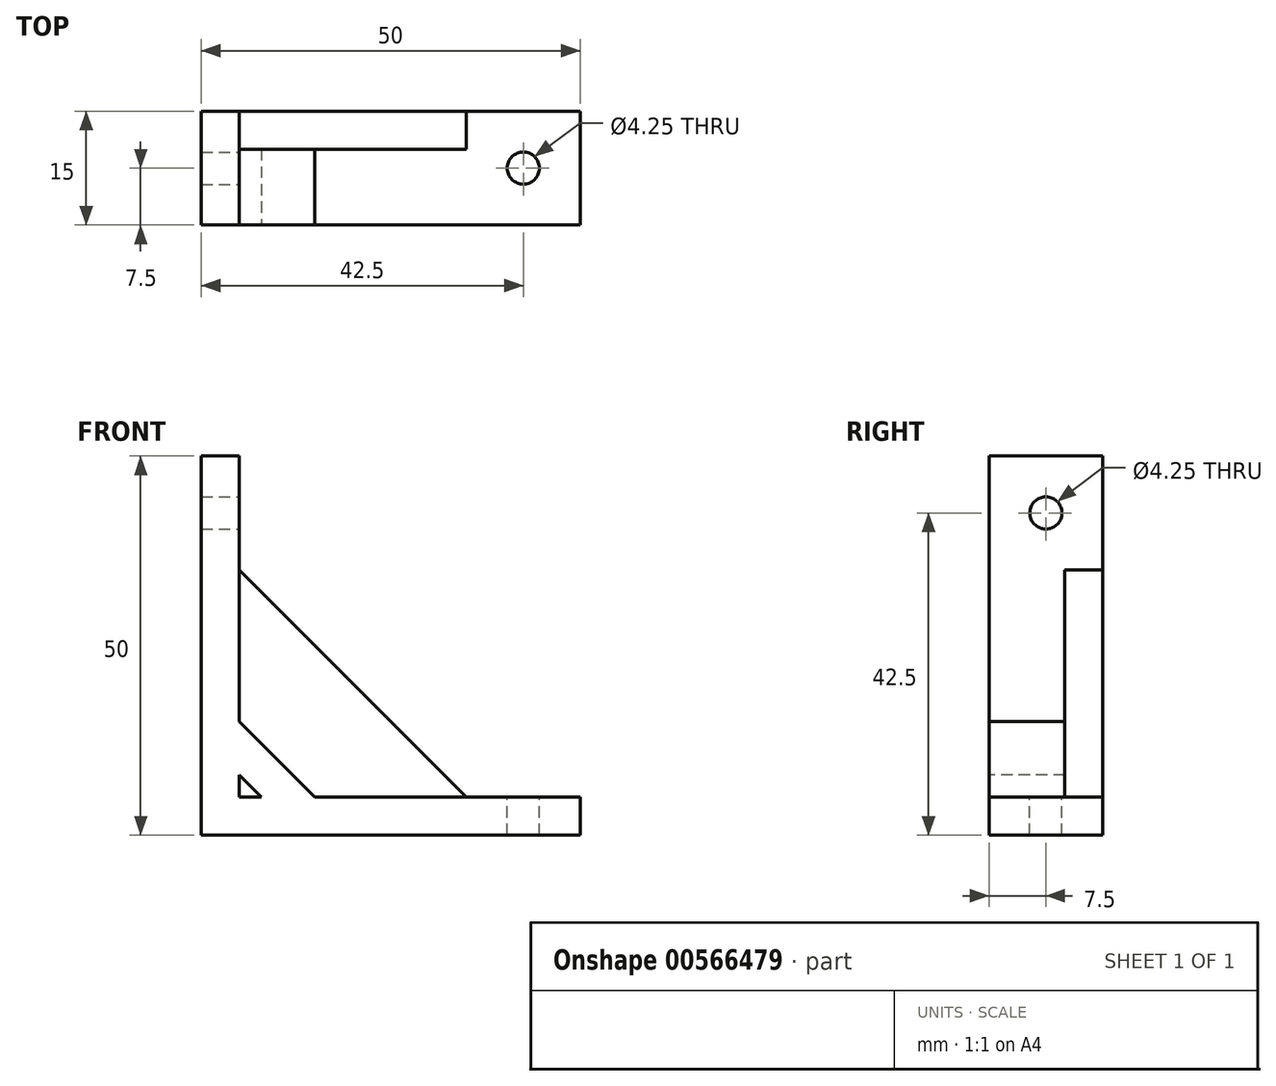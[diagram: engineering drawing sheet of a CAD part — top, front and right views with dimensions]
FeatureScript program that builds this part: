
annotation { "Feature Type Name" : "Feature", "Feature Type Description" : "" }
export const myFeature = defineFeature(function(context is Context, id is Id, definition is map)
    precondition{}
    {
        {
            var Q0;
            Q0=qCreatedBy(makeId("Front.planeOp"),FACE);
            var sketch = newSketch(context, id + "F0", { "sketchPlane" : qUnion([Q0])});
            skLineSegment(sketch, "E0", {"start": v(0, 50) * mm, "end": v(0, 0) * mm});
            skLineSegment(sketch, "E1", {"start": v(0, 0) * mm, "end": v(50, 0) * mm});
            skLineSegment(sketch, "E2", {"start": v(50, 0) * mm, "end": v(50, 5) * mm});
            skLineSegment(sketch, "E3", {"start": v(50, 5) * mm, "end": v(35, 5) * mm});
            skLineSegment(sketch, "E4", {"start": v(35, 5) * mm, "end": v(5, 35) * mm});
            skLineSegment(sketch, "E5", {"start": v(5, 35) * mm, "end": v(5, 50) * mm});
            skLineSegment(sketch, "E6", {"start": v(5, 50) * mm, "end": v(0, 50) * mm});
            skSolve(sketch);
        }
        {
            var Q0;
            Q0=qSketchRegion(id+"F0",true);
            extrude(context, id + "F1", {"entities" : qUnion([Q0]), "depth" : 15 * mm});
        }
        {
            var Q0;
            Q0=makeQuery(id+"F1.opExtrude","SWEPT_FACE",FACE,{"disambiguationData":[OSD([sQuery(id+"F0.wireOp",EDGE,"E3")])]});
            var sketch = newSketch(context, id + "F2", { "sketchPlane" : qUnion([Q0])});
            skCircle(sketch, "E7", {"center": v(42.5, -7.5) * mm, "radius": 2.12 * mm});
            skSolve(sketch);
        }
        {
            var Q0;
            Q0=qSketchRegion(id+"F2",true);
            extrude(context, id + "F3", {"entities" : qUnion([Q0]), "operationType" : NewBodyOperationType.REMOVE, "oppositeDirection" : true, "depth" : 25 * mm});
        }
        {
            var Q0;
            Q0=makeQuery(id+"F1.opExtrude","SWEPT_FACE",FACE,{"disambiguationData":[OSD([sQuery(id+"F0.wireOp",EDGE,"E5")])]});
            var sketch = newSketch(context, id + "F4", { "sketchPlane" : qUnion([Q0])});
            skCircle(sketch, "E8", {"center": v(-7.5, 42.5) * mm, "radius": 2.12 * mm});
            skPoint(sketch, "E8.centerSnap0", {"position": v(0, 42.5) * mm});
            skSolve(sketch);
        }
        {
            var Q0;
            Q0=qSketchRegion(id+"F4",true);
            extrude(context, id + "F5", {"entities" : qUnion([Q0]), "operationType" : NewBodyOperationType.REMOVE, "oppositeDirection" : true, "depth" : 25 * mm});
        }
        {
            var Q0;
            Q0=makeQuery(id+"F1.opExtrude","CAP_FACE",FACE,{"disambiguationData":[OSD([sQuery(id+"F0.wireOp",EDGE,"E0"),sQuery(id+"F0.wireOp",EDGE,"E1"),sQuery(id+"F0.wireOp",EDGE,"E2"),sQuery(id+"F0.wireOp",EDGE,"E3"),sQuery(id+"F0.wireOp",EDGE,"E4"),sQuery(id+"F0.wireOp",EDGE,"E5"),sQuery(id+"F0.wireOp",EDGE,"E6")])],"isStart":false});
            var sketch = newSketch(context, id + "F6", { "sketchPlane" : qUnion([Q0])});
            skLineSegment(sketch, "E9", {"start": v(5, 35) * mm, "end": v(35, 5) * mm});
            skLineSegment(sketch, "E10", {"start": v(35, 5) * mm, "end": v(15, 5) * mm});
            skLineSegment(sketch, "E11", {"start": v(15, 5) * mm, "end": v(5, 15) * mm});
            skLineSegment(sketch, "E12", {"start": v(5, 15) * mm, "end": v(5, 35) * mm});
            skSolve(sketch);
        }
        {
            var Q0;
            Q0=qSketchRegion(id+"F6",true);
            extrude(context, id + "F7", {"entities" : qUnion([Q0]), "operationType" : NewBodyOperationType.REMOVE, "oppositeDirection" : true, "depth" : 10 * mm});
        }
        {
            var Q0;
            Q0=makeQuery(id+"F1.opExtrude","CAP_FACE",FACE,{"disambiguationData":[OSD([sQuery(id+"F0.wireOp",EDGE,"E0"),sQuery(id+"F0.wireOp",EDGE,"E1"),sQuery(id+"F0.wireOp",EDGE,"E2"),sQuery(id+"F0.wireOp",EDGE,"E3"),sQuery(id+"F0.wireOp",EDGE,"E4"),sQuery(id+"F0.wireOp",EDGE,"E5"),sQuery(id+"F0.wireOp",EDGE,"E6")])],"isStart":false});
            var sketch = newSketch(context, id + "F8", { "sketchPlane" : qUnion([Q0])});
            skLineSegment(sketch, "E13", {"start": v(5, 7.93) * mm, "end": v(7.93, 5) * mm});
            skLineSegment(sketch, "E14", {"start": v(7.93, 5) * mm, "end": v(5, 5) * mm});
            skLineSegment(sketch, "E15", {"start": v(5, 5) * mm, "end": v(5, 7.93) * mm});
            skSolve(sketch);
        }
        {
            var Q0;
            Q0=qSketchRegion(id+"F8",true);
            extrude(context, id + "F9", {"entities" : qUnion([Q0]), "operationType" : NewBodyOperationType.REMOVE, "oppositeDirection" : true, "depth" : 10 * mm});
        }
    });
